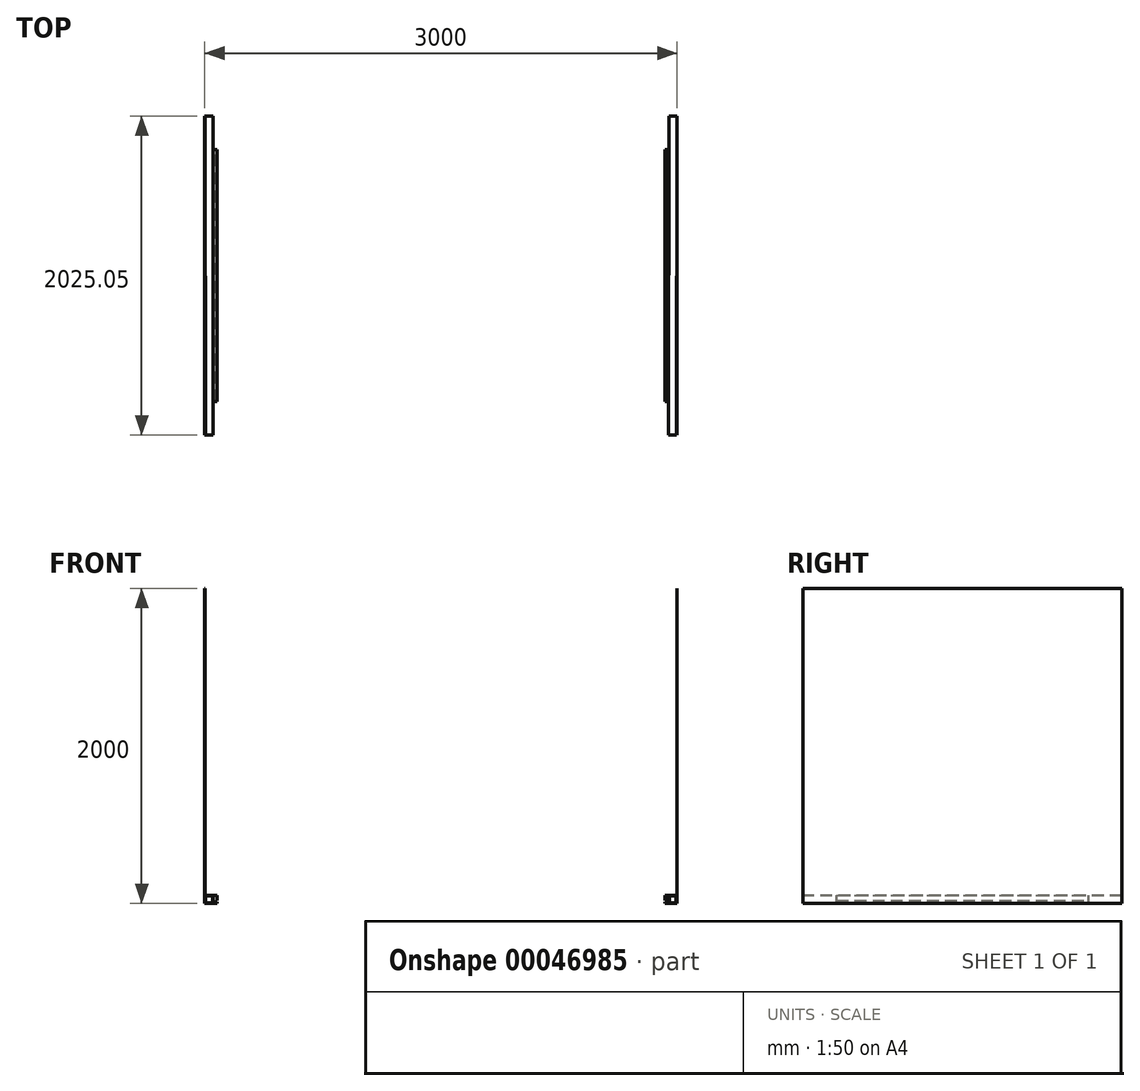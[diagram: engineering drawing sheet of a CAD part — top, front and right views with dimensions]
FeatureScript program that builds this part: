
annotation { "Feature Type Name" : "Feature", "Feature Type Description" : "" }
export const myFeature = defineFeature(function(context is Context, id is Id, definition is map)
    precondition{}
    {
        {
            var Q0;
            Q0=qCreatedBy(makeId("Top.planeOp"),FACE);
            var sketch = newSketch(context, id + "F0", { "sketchPlane" : qUnion([Q0])});
            skLineSegment(sketch, "E0.rect.bottom", {"start": v(-1, 1012.5) * mm, "end": v(1, 1012.5) * mm});
            skLineSegment(sketch, "E0.rect.left", {"start": v(-1, 1012.5) * mm, "end": v(-1, -1012.5) * mm});
            skLineSegment(sketch, "E0.rect.right", {"start": v(1, 1012.5) * mm, "end": v(1, -1012.5) * mm});
            skPoint(sketch, "E0.rect.middle", {"position": v(0, 0) * mm});
            skLineSegment(sketch, "E1", {"start": v(-1, -1012.5) * mm, "end": v(1, -1012.5) * mm});
            skSolve(sketch);
        }
        {
            var Q0;
            Q0=qSketchRegion(id+"F0",true);
            extrude(context, id + "F1", {"entities" : qUnion([Q0]), "depth" : 2000 * mm});
        }
        {
            var Q0;
            Q0=makeQuery(id+"F1.opExtrude","SWEPT_FACE",FACE,{"disambiguationData":[OSD([sQuery(id+"F0.wireOp",EDGE,"E1")])]});
            var sketch = newSketch(context, id + "F2", { "sketchPlane" : qUnion([Q0])});
            skLineSegment(sketch, "E2.rect.bottom", {"start": v(-2.01, 0) * mm, "end": v(-52.01, 0) * mm});
            skLineSegment(sketch, "E2.rect.top", {"start": v(-2.01, 50) * mm, "end": v(-52.01, 50) * mm});
            skLineSegment(sketch, "E2.rect.left", {"start": v(-2.01, 0) * mm, "end": v(-2.01, 50) * mm});
            skLineSegment(sketch, "E2.rect.right", {"start": v(-52.01, 0) * mm, "end": v(-52.01, 50) * mm});
            skPoint(sketch, "E2.rect.middle", {"position": v(-27.01, 25) * mm});
            skLineSegment(sketch, "E3.rect.bottom", {"start": v(-50.01, 48) * mm, "end": v(-4.01, 48) * mm});
            skLineSegment(sketch, "E3.rect.top", {"start": v(-50.01, 2) * mm, "end": v(-4.01, 2) * mm});
            skLineSegment(sketch, "E3.rect.left", {"start": v(-50.01, 48) * mm, "end": v(-50.01, 2) * mm});
            skLineSegment(sketch, "E3.rect.right", {"start": v(-4.01, 48) * mm, "end": v(-4.01, 2) * mm});
            skSolve(sketch);
        }
        {
            var Q0;
            Q0=qSketchRegion(id+"F2",true);
            extrude(context, id + "F3", {"entities" : qUnion([Q0]), "oppositeDirection" : true, "depth" : 2025 * mm});
        }
        {
            var Q0;
            Q0=makeQuery(id+"F1.opExtrude","SWEPT_FACE",FACE,{"disambiguationData":[OSD([sQuery(id+"F0.wireOp",EDGE,"E0.rect.right")])]});
            cPlane(context, id + "F4", {"entities" : qUnion([Q0]), "cplaneType" : CPlaneType.OFFSET, "offset" : 1500 * mm, "oppositeDirection" : true, "width" : 150 * mm, "height" : 150 * mm});
        }
        {
            var Q0;
            Q0=makeQuery(id+"F1.opExtrude","SWEPT_BODY",BODY,{"disambiguationData":[OSD([sQuery(id+"F0.wireOp",EDGE,"E0.rect.bottom"),sQuery(id+"F0.wireOp",EDGE,"E0.rect.left"),sQuery(id+"F0.wireOp",EDGE,"E0.rect.right"),sQuery(id+"F0.wireOp",EDGE,"E1")])]});
            var Q1;
            Q1=makeQuery(id+"F3.opExtrude","SWEPT_BODY",BODY,{"disambiguationData":[OSD([sQuery(id+"F2.wireOp",EDGE,"E2.rect.bottom"),sQuery(id+"F2.wireOp",EDGE,"E2.rect.top"),sQuery(id+"F2.wireOp",EDGE,"E2.rect.left"),sQuery(id+"F2.wireOp",EDGE,"E2.rect.right"),sQuery(id+"F2.wireOp",EDGE,"E3.rect.bottom"),sQuery(id+"F2.wireOp",EDGE,"E3.rect.top"),sQuery(id+"F2.wireOp",EDGE,"E3.rect.left"),sQuery(id+"F2.wireOp",EDGE,"E3.rect.right")])]});
            var Q2;
            Q2=qCreatedBy(id+"F4.planeOp",FACE);
            mirror(context, id + "F5", {"entities" : qUnion([Q0, Q1]), "mirrorPlane" : qUnion([Q2])});
        }
        {
            var Q0;
            Q0=qCreatedBy(makeId("Front.planeOp"),FACE);
            var sketch = newSketch(context, id + "F6", { "sketchPlane" : qUnion([Q0])});
            skLineSegment(sketch, "E4", {"start": v(-53.02, 50) * mm, "end": v(-53.02, 0) * mm});
            skLineSegment(sketch, "E5", {"start": v(-53.02, 0) * mm, "end": v(-77.27, 0) * mm});
            skLineSegment(sketch, "E6", {"start": v(-77.27, 10) * mm, "end": v(-67.27, 10) * mm});
            skLineSegment(sketch, "E7", {"start": v(-67.27, 10) * mm, "end": v(-67.27, 20) * mm});
            skLineSegment(sketch, "E8", {"start": v(-67.27, 20) * mm, "end": v(-77.27, 20) * mm});
            skLineSegment(sketch, "E9", {"start": v(-77.27, 20) * mm, "end": v(-77.27, 50) * mm});
            skLineSegment(sketch, "E10", {"start": v(-77.27, 50) * mm, "end": v(-53.02, 50) * mm});
            skLineSegment(sketch, "E11", {"start": v(-77.27, 10) * mm, "end": v(-77.27, 0) * mm});
            skLineSegment(sketch, "E12.MirrorCS", {"start": v(-2930.73, 20) * mm, "end": v(-2920.73, 20) * mm});
            skLineSegment(sketch, "E13.MirrorCS", {"start": v(-2930.73, 10) * mm, "end": v(-2930.73, 20) * mm});
            skLineSegment(sketch, "E14.MirrorCS", {"start": v(-2920.73, 20) * mm, "end": v(-2920.73, 50) * mm});
            skLineSegment(sketch, "E15.MirrorCS", {"start": v(-2920.73, 10) * mm, "end": v(-2930.73, 10) * mm});
            skLineSegment(sketch, "E16.MirrorCS", {"start": v(-2920.73, 10) * mm, "end": v(-2920.73, 0) * mm});
            skLineSegment(sketch, "E17.MirrorCS", {"start": v(-2944.98, 50) * mm, "end": v(-2944.98, 0) * mm});
            skLineSegment(sketch, "E18.MirrorCS", {"start": v(-2920.73, 50) * mm, "end": v(-2944.98, 50) * mm});
            skLineSegment(sketch, "E19.MirrorCS", {"start": v(-2944.98, 0) * mm, "end": v(-2920.73, 0) * mm});
            skSolve(sketch);
        }
        {
            var Q0;
            Q0=makeQuery(id+"F6.imprint","IMPRINT",FACE,{"disambiguationData":[TD([[makeQuery(id+"F6.imprint","IMPRINT",EDGE,{"derivedFrom":sQuery(id+"F6.wireOp",EDGE,"E4")}),-1.0]])]});
            var Q1;
            Q1=makeQuery(id+"F6.imprint","IMPRINT",FACE,{"disambiguationData":[TD([[makeQuery(id+"F6.imprint","IMPRINT",EDGE,{"derivedFrom":sQuery(id+"F6.wireOp",EDGE,"E16.MirrorCS")}),-1.0]])]});
            extrude(context, id + "F7", {"entities" : qUnion([Q0, Q1]), "endBound" : BoundingType.SYMMETRIC, "depth" : 1600 * mm});
        }
    });
